# Revit family: Sanitary_Taps-Mixers_hansgrohe_31460XXX-Metris-S-Single-lever-bath-mixe___
name_source: partatom
category: Plumbing Fixtures
revit_build: Autodesk Revit 2018 (Build: 20170223_1515(x64)
units: mm (PartAtom-declared; Revit-internal decimal feet)

## family parameters
Always vertical = No
Cut with Voids When Loaded = No
OmniClass Number = 23.45.05.14
OmniClass Title = Plumbing Fixtures - Sanitary Washing Units
Part Type = Normal
Room Calculation Point = No
Round Connector Dimension = Use Diameter
Shared = No
Work Plane-Based = Yes

## types (1)
- 000 Chrome
    BIMobject category = Taps & Mixers
    Default Elevation = 1219 mm
    Description = Metris S Single lever bath mixer for exposed installation
    Edition number = 1
    IFC Classification = Valve
    Manufacturer = Hansgrohe
    Manufacturer name = hansgrohe
    Masterformat 2014 Code = 22 41 39
    Masterformat 2014 Description = Residential Faucets, Supplies, and Trim
    Material 1 = Hansgrohe - Metal - 000 Chrome
    Model = 31460XXX
    NBS Reference Code = 35-06-07
    NBS Reference Description = Bath Water Supply Fittings
    OmniClass Code = 23-31 11 00
    OmniClass Description = Faucets
    Product Guid = 95672146-4d28-4b4c-af9a-d72c9caca9fa
    Product SKU = 31460XXX
    Product data url = https://bimobject.com
    Product family = Metris S
    Product group = Bath mixers
    Product name = 31460XXX Metris S Single lever bath mixer for exposed installation
    QR code = https://www.bimobject.com
    URL = https://www.hansgrohe.com
    Uniclass 2015 Code = Pr_40_20_87
    Uniclass 2015 Name = Taps and water supply outlet fittings
    Uniformat II Code = D2010
    Uniformat II Description = Plumbing Fixtures
